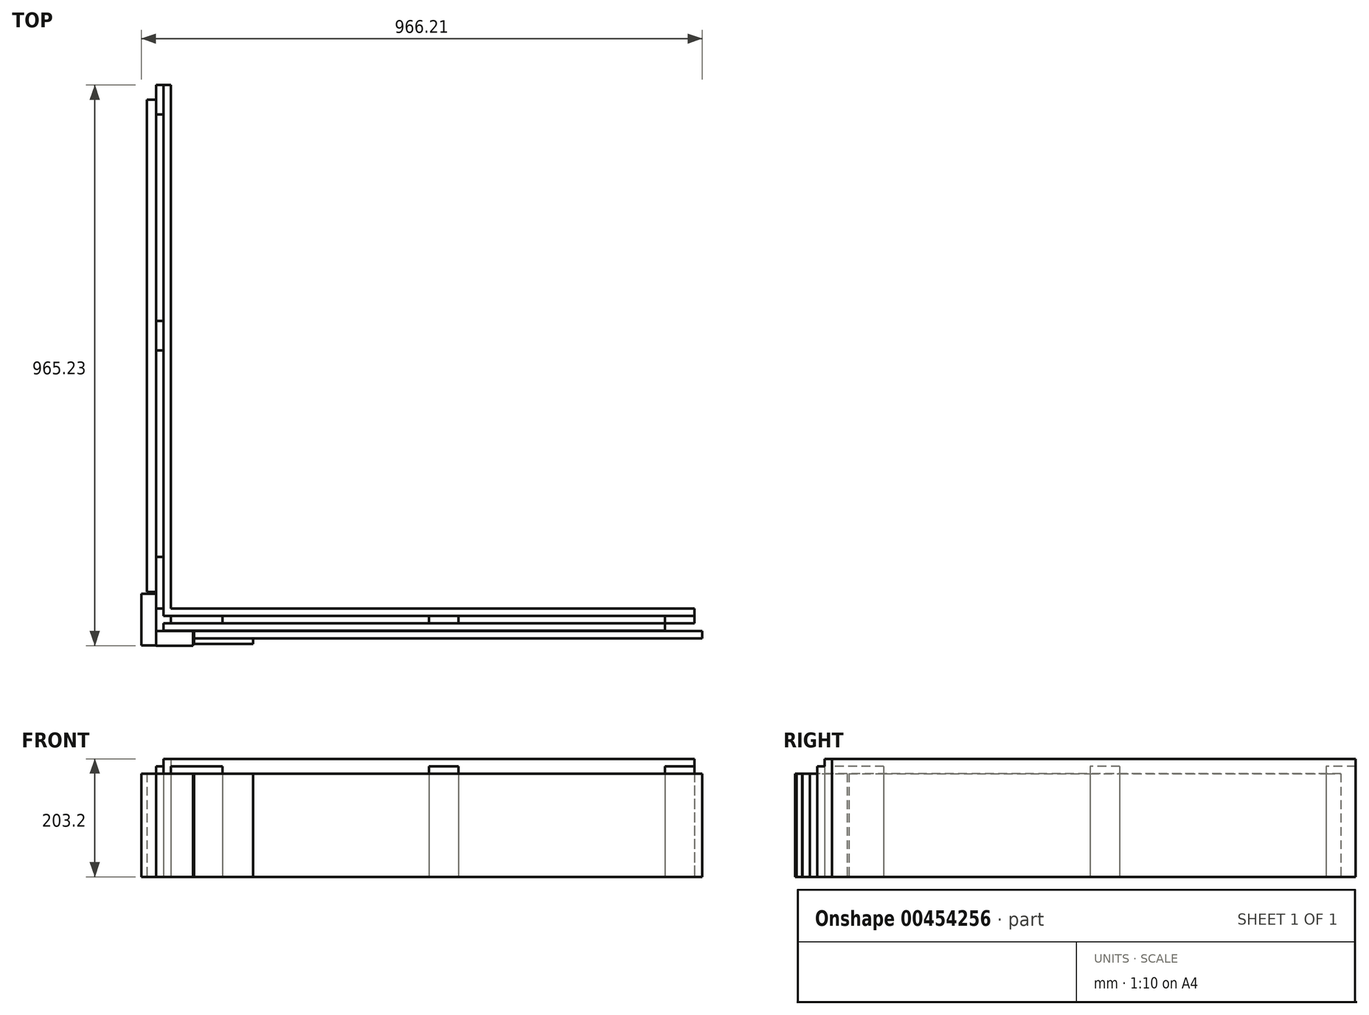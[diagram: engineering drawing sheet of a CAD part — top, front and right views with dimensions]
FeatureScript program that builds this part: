
annotation { "Feature Type Name" : "Feature", "Feature Type Description" : "" }
export const myFeature = defineFeature(function(context is Context, id is Id, definition is map)
    precondition{}
    {
        {
            var Q0;
            Q0=qCreatedBy(makeId("Top.planeOp"),FACE);
            var sketch = newSketch(context, id + "F0", { "sketchPlane" : qUnion([Q0])});
            skLineSegment(sketch, "E0", {"start": v(0, 0) * mm, "end": v(0, 914.4) * mm});
            skLineSegment(sketch, "E1", {"start": v(0, 914.4) * mm, "end": v(12.7, 914.4) * mm});
            skLineSegment(sketch, "E2", {"start": v(12.7, 914.4) * mm, "end": v(12.7, 12.7) * mm});
            skLineSegment(sketch, "E3", {"start": v(12.7, 12.7) * mm, "end": v(914.4, 12.7) * mm});
            skLineSegment(sketch, "E4", {"start": v(914.4, 12.7) * mm, "end": v(914.4, 0) * mm});
            skLineSegment(sketch, "E5", {"start": v(914.4, 0) * mm, "end": v(0, 0) * mm});
            skSolve(sketch);
        }
        {
            var Q0;
            Q0 = qSketchRegion(id + "F0", true);
            extrude(context, id + "F1", {"entities" : qUnion([Q0]), "depth" : 203.2 * mm});
        }
        {
            var Q0;
            Q0=qCreatedBy(makeId("Top.planeOp"),FACE);
            var sketch = newSketch(context, id + "F2", { "sketchPlane" : qUnion([Q0])});
            skLineSegment(sketch, "E6", {"start": v(457.2, 0) * mm, "end": v(457.2, -12.7) * mm});
            skLineSegment(sketch, "E7", {"start": v(457.2, -12.7) * mm, "end": v(508, -12.7) * mm});
            skLineSegment(sketch, "E8", {"start": v(508, -12.7) * mm, "end": v(508, 0) * mm});
            skLineSegment(sketch, "E9", {"start": v(863.6, 0) * mm, "end": v(863.6, -12.7) * mm});
            skLineSegment(sketch, "E10", {"start": v(863.6, -12.7) * mm, "end": v(914.4, -12.7) * mm});
            skLineSegment(sketch, "E11", {"start": v(914.4, -12.7) * mm, "end": v(914.4, 0) * mm});
            skLineSegment(sketch, "E12", {"start": v(12.7, 0) * mm, "end": v(12.7, -12.7) * mm});
            skLineSegment(sketch, "E13", {"start": v(12.7, -12.7) * mm, "end": v(101.6, -12.7) * mm});
            skLineSegment(sketch, "E14", {"start": v(101.6, -12.7) * mm, "end": v(101.6, 0) * mm});
            skLineSegment(sketch, "E15", {"start": v(-12.7, 12.7) * mm, "end": v(-12.7, 101.6) * mm});
            skLineSegment(sketch, "E16", {"start": v(-12.7, 101.6) * mm, "end": v(0, 101.6) * mm});
            skLineSegment(sketch, "E17", {"start": v(0, 457.2) * mm, "end": v(-12.7, 457.2) * mm});
            skLineSegment(sketch, "E18", {"start": v(-12.7, 457.2) * mm, "end": v(-12.7, 508) * mm});
            skLineSegment(sketch, "E19", {"start": v(-12.7, 508) * mm, "end": v(0, 508) * mm});
            skLineSegment(sketch, "E20", {"start": v(0, 863.6) * mm, "end": v(-12.7, 863.6) * mm});
            skLineSegment(sketch, "E21", {"start": v(-12.7, 863.6) * mm, "end": v(-12.7, 914.4) * mm});
            skLineSegment(sketch, "E22", {"start": v(-12.7, 914.4) * mm, "end": v(0, 914.4) * mm});
            skLineSegment(sketch, "E23", {"start": v(-66.14, 512.38) * mm, "end": v(-66.14, -106.7) * mm, "construction": true});
            skLineSegment(sketch, "E24", {"start": v(0, 914.4) * mm, "end": v(0, 863.6) * mm});
            skLineSegment(sketch, "E25", {"start": v(0, 508) * mm, "end": v(0, 457.2) * mm});
            skLineSegment(sketch, "E26", {"start": v(0, 101.6) * mm, "end": v(0, 12.7) * mm});
            skLineSegment(sketch, "E27", {"start": v(12.7, 0) * mm, "end": v(101.6, 0) * mm});
            skLineSegment(sketch, "E28", {"start": v(457.2, 0) * mm, "end": v(508, 0) * mm});
            skLineSegment(sketch, "E29", {"start": v(863.6, 0) * mm, "end": v(914.4, 0) * mm});
            skLineSegment(sketch, "E30", {"start": v(-12.7, 12.7) * mm, "end": v(0, 12.7) * mm});
            skSolve(sketch);
        }
        {
            var Q0;
            Q0 = qSketchRegion(id + "F2", true);
            var Q1;
            Q1=makeQuery(id+"F1.opExtrude","CAP_FACE",FACE,{"disambiguationData":[OSD([sQuery(id+"F0.wireOp",EDGE,"E0"),sQuery(id+"F0.wireOp",EDGE,"E1"),sQuery(id+"F0.wireOp",EDGE,"E2"),sQuery(id+"F0.wireOp",EDGE,"E3"),sQuery(id+"F0.wireOp",EDGE,"E4"),sQuery(id+"F0.wireOp",EDGE,"E5")])],"isStart":false});
            extrude(context, id + "F3", {"entities" : qUnion([Q0]), "operationType" : NewBodyOperationType.ADD, "endBoundEntityFace" : qUnion([Q1]), "depth" : 190.5 * mm});
        }
        {
            var Q0;
            Q0=qCreatedBy(makeId("Top.planeOp"),FACE);
            var sketch = newSketch(context, id + "F4", { "sketchPlane" : qUnion([Q0])});
            skLineSegment(sketch, "E31", {"start": v(-12.95, -50.57) * mm, "end": v(-38.35, -50.57) * mm});
            skLineSegment(sketch, "E32", {"start": v(-38.35, -50.57) * mm, "end": v(-38.35, 38.33) * mm});
            skLineSegment(sketch, "E33", {"start": v(-38.35, 38.33) * mm, "end": v(-12.95, 38.33) * mm});
            skLineSegment(sketch, "E34", {"start": v(-12.7, -25.43) * mm, "end": v(50.8, -25.43) * mm});
            skLineSegment(sketch, "E35", {"start": v(50.8, -25.43) * mm, "end": v(50.8, -50.83) * mm});
            skLineSegment(sketch, "E36", {"start": v(50.8, -50.83) * mm, "end": v(-12.7, -50.83) * mm});
            skLineSegment(sketch, "E37", {"start": v(-12.7, -50.83) * mm, "end": v(-12.7, -25.43) * mm});
            skLineSegment(sketch, "E38", {"start": v(-12.95, 38.33) * mm, "end": v(-12.95, -50.57) * mm});
            skSolve(sketch);
        }
        {
            var Q0;
            Q0=makeQuery(id+"F4.imprint","IMPRINT",FACE,{"disambiguationData":[TD([[makeQuery(id+"F4.imprint","IMPRINT",EDGE,{"derivedFrom":sQuery(id+"F4.wireOp",EDGE,"E31")}),-1.0]])]});
            var Q1;
            Q1=makeQuery(id+"F4.imprint","IMPRINT",FACE,{"disambiguationData":[TD([[makeQuery(id+"F4.imprint","IMPRINT",EDGE,{"derivedFrom":sQuery(id+"F4.wireOp",EDGE,"E34")}),-1.0]])]});
            extrude(context, id + "F5", {"entities" : qUnion([Q0, Q1]), "operationType" : NewBodyOperationType.ADD, "depth" : 177.8 * mm});
        }
        {
            var Q0;
            Q0=qCreatedBy(makeId("Top.planeOp"),FACE);
            var sketch = newSketch(context, id + "F6", { "sketchPlane" : qUnion([Q0])});
            skLineSegment(sketch, "E39", {"start": v(-12.7, 41.5) * mm, "end": v(-12.7, 889) * mm});
            skLineSegment(sketch, "E40", {"start": v(-12.7, 889) * mm, "end": v(-28.58, 889) * mm});
            skLineSegment(sketch, "E41", {"start": v(-28.58, 889) * mm, "end": v(-28.57, 41.5) * mm});
            skLineSegment(sketch, "E42", {"start": v(-28.57, 41.5) * mm, "end": v(-12.7, 41.5) * mm});
            skSolve(sketch);
        }
        {
            var Q0;
            Q0 = qSketchRegion(id + "F6", true);
            extrude(context, id + "F7", {"entities" : qUnion([Q0]), "operationType" : NewBodyOperationType.ADD, "depth" : 177.8 * mm});
        }
        {
            var Q0;
            Q0=qCreatedBy(makeId("Top.planeOp"),FACE);
            var sketch = newSketch(context, id + "F8", { "sketchPlane" : qUnion([Q0])});
            skLineSegment(sketch, "E43", {"start": v(0, -12.7) * mm, "end": v(0, -25.4) * mm});
            skLineSegment(sketch, "E44", {"start": v(0, -25.4) * mm, "end": v(863.6, -25.4) * mm});
            skLineSegment(sketch, "E45", {"start": v(863.6, -25.4) * mm, "end": v(863.6, -12.7) * mm});
            skLineSegment(sketch, "E46", {"start": v(863.6, -12.7) * mm, "end": v(0, -12.7) * mm});
            skSolve(sketch);
        }
        {
            var Q0;
            Q0 = qSketchRegion(id + "F8", true);
            extrude(context, id + "F9", {"entities" : qUnion([Q0]), "depth" : 177.8 * mm});
        }
        {
            var Q0;
            Q0=qCreatedBy(makeId("Top.planeOp"),FACE);
            var sketch = newSketch(context, id + "F10", { "sketchPlane" : qUnion([Q0])});
            skLineSegment(sketch, "E47.bottom", {"start": v(52.39, -25.65) * mm, "end": v(927.86, -25.65) * mm});
            skLineSegment(sketch, "E47.top", {"start": v(52.39, -38.35) * mm, "end": v(927.86, -38.35) * mm});
            skLineSegment(sketch, "E47.left", {"start": v(52.39, -25.65) * mm, "end": v(52.39, -38.35) * mm});
            skLineSegment(sketch, "E47.right", {"start": v(927.86, -25.65) * mm, "end": v(927.86, -38.35) * mm});
            skLineSegment(sketch, "E48.bottom", {"start": v(52.39, -38.6) * mm, "end": v(153.99, -38.6) * mm});
            skLineSegment(sketch, "E48.top", {"start": v(52.39, -48.13) * mm, "end": v(153.99, -48.13) * mm});
            skLineSegment(sketch, "E48.left", {"start": v(52.39, -38.6) * mm, "end": v(52.39, -48.13) * mm});
            skLineSegment(sketch, "E48.right", {"start": v(153.99, -38.6) * mm, "end": v(153.99, -48.13) * mm});
            skSolve(sketch);
        }
        {
            var Q0;
            Q0 = qSketchRegion(id + "F10", true);
            extrude(context, id + "F11", {"entities" : qUnion([Q0]), "depth" : 177.8 * mm});
        }
    });
